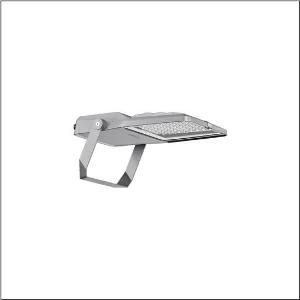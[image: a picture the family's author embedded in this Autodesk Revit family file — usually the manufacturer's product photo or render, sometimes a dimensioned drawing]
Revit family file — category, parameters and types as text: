
# Revit family: floodlight_fl_21_iq_mini___pl64_5xa7772b2e1a_9a08
name_source: partatom
category: Lighting Fixtures
units: mm (PartAtom-declared; Revit-internal decimal feet)

## family parameters
Cut with Voids When Loaded = No
Host = Face
Light Source = No
Part Type = Normal
Room Calculation Point = No
Round Connector Dimension = Use Diameter
Shared = No

## types (1)
- --- (1 x LED, 6020 lm, 45.5 W, 3000K)
    Apparent Load = 46 VA
    CIE Flux Codes = 28 80 98 100 100
    Color Rendering = 70
    Color Temperature = 3000K
    Default Elevation = 1800 mm
    Description = Floodlight FL 21 iQ mini, floodlight, primary light control with lens, of PMMA, primary optical cover: protective disc, of toughened safety glass, transparent, light distribution: PL64, light emission: direct distribution, installation type: surface-mounted, LED, High Power LED, rated luminous flux: 6.020lm, luminous efficacy: 132lm/W, light colour: 730, colour temperature: 3000K, control: Street-Remote, Auto-Match, Temp-Guard, Night-Set, Smart-Wire, Desk-Remote (wireless, voltage-free reading and setting of iQ features in the workshop via application-optimized NFC function/RFID function), optimised constant luminous flux control (CLO 2.0), with terminal, 6-pole, mains connection: 220..240V, AC, 50/60Hz, start of lifetime: 46W, end of service life: 48W, reduction: 22W, luminaire housing, of diecast aluminium, powder-coated, Siteco® metallic grey (DB 702S), corrosivity category C5 mid according to DIN EN ISO 12944, sealing non-destructively replaceable, mounting bracket, of steel, galvanised, powder-coated, Siteco® metallic grey (DB 702S), protection rating (complete): IP66, insulation class (complete): insulation class II (safety insulation), certification: CE, ENEC, VDE, protection symbol: D, impact resistance: IK08, permissible operating ambient temperature: -40..+40°C, permissible operating ambient temperature for outdoor applications: -40..+50°C, standard: DIN EN 12944, LABS conformity tested according to VDMA 24364:2018-05, packaging unit: 1 piece

Light Distribution: PL64
    Height = 70 mm
    Lamp = 1 x LED
    Lamp Light Flux = 6020 lm
    Lamp Power = 45.5 W
    Lamp count = 1
    Length = 485 mm
    Luminous efficacy = 132 lm/W
    Manufacturer = Siteco
    ModVariant = No
    Model = 5XA7772B2E1A
    Number of Poles = 1
    OnlyDefault = Yes
    Power Factor = 1
    Product Name = Floodlight FL 21 iQ mini | PL64
    Product group = floodlight | pylon annexe
    ProductGroupID = 6200
    Protection Class = Protection class II
    Protection Degree = IP 66
    RLX_Detail_Level = 1
    RLX_Emergency_Light_Flux = 0 lm
    RLX_Emergency_Type = 0
    RLX_Emergency_Type_DB = No
    RlxData = <blob elided: 96017 chars, md5=5a3ddadb>
    Socket = socket
    Standby Power = 0 W
    System Light Flux = 6020 lm
    System Power = 46 W
    Type Comments = factory setting: luminous flux: 100 % | dim-lin: 254 | 463 mA
    Type Image = l_1006845.jpg
    URL = http://relux.com
    VarID = @adj_117125
    Voltage = 0 V
    Weight = 0.00 kg
    Width = 337 mm

## geometry (parser evidence)
native form markers: Blend x4, Sweep x13
no freeform markers — native parametric forms only
